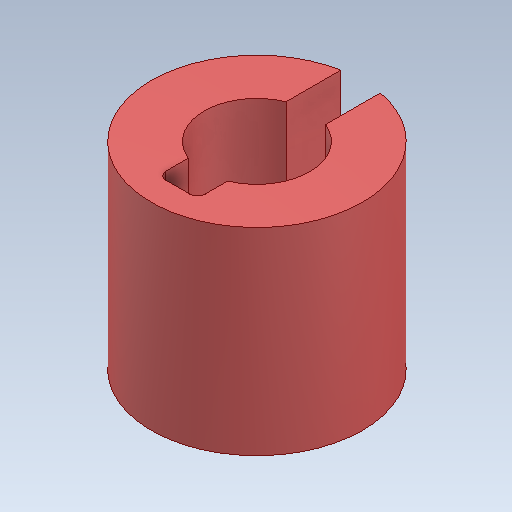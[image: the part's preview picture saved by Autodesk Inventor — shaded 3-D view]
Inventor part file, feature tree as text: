
AUTODESK INVENTOR PART (.ipt)
format: ipt  version: 2020 (Build 240168000, 168)  size: 110,080 bytes
history: native  units: in
note: dims shown in document units (in); Inventor stores cm internally (conversion verified against a paired STEP export)
features: fillet x1
ambient origin geometry x8: Origin, YZ Plane, XZ Plane, XY Plane, X Axis, Y Axis, Z Axis, Center Point
bodies: Solid1 (feature_tree)
feature tree (1):
  fillet  "Fillet1"  [1 undecoded]
note: 1 required parameter value undecoded (feature->parameter linkage not recoverable at this tier; creation-order binding heuristic only, values carry confidence <= 0.55)
